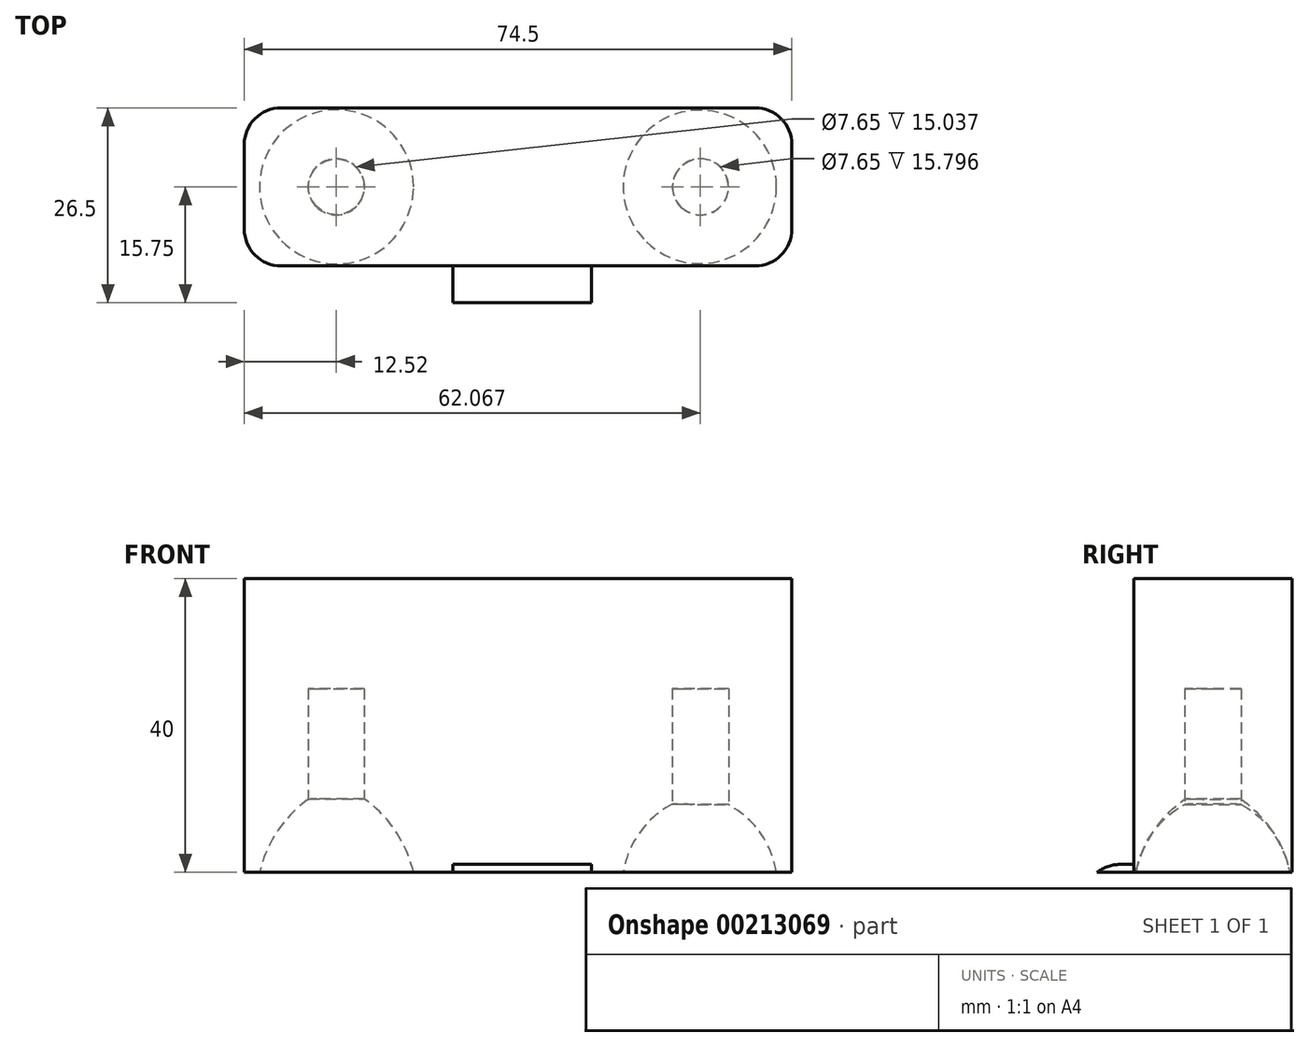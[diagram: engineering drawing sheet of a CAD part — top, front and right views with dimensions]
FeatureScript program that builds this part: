
annotation { "Feature Type Name" : "Feature", "Feature Type Description" : "" }
export const myFeature = defineFeature(function(context is Context, id is Id, definition is map)
    precondition{}
    {
        {
            var Q0;
            Q0=qCreatedBy(makeId("Top.planeOp"),FACE);
            var sketch = newSketch(context, id + "F0", { "sketchPlane" : qUnion([Q0])});
            skLineSegment(sketch, "E0.bottom", {"start": v(-37.25, 10.75) * mm, "end": v(37.25, 10.75) * mm});
            skLineSegment(sketch, "E0.top", {"start": v(-37.25, -10.75) * mm, "end": v(37.25, -10.75) * mm});
            skLineSegment(sketch, "E0.left", {"start": v(-37.25, 10.75) * mm, "end": v(-37.25, -10.75) * mm});
            skLineSegment(sketch, "E0.right", {"start": v(37.25, 10.75) * mm, "end": v(37.25, -10.75) * mm});
            skPoint(sketch, "E1", {"position": v(-37.25, 0) * mm});
            skPoint(sketch, "E2", {"position": v(0, 10.75) * mm});
            skPoint(sketch, "E3", {"position": v(0, -10.75) * mm});
            skPoint(sketch, "E4", {"position": v(37.25, 0) * mm});
            skCircle(sketch, "E5", {"center": v(-24.7, 0) * mm, "radius": 10.55 * mm});
            skCircle(sketch, "E6", {"center": v(24.76, 0) * mm, "radius": 10.55 * mm});
            skLineSegment(sketch, "E7", {"start": v(-24.7, 0) * mm, "end": v(24.76, 0) * mm});
            skSolve(sketch);
        }
        {
            var Q0;
            Q0=makeQuery(id+"F0.imprint","IMPRINT",FACE,{"disambiguationData":[TD([[makeQuery(id+"F0.imprint","IMPRINT",EDGE,{"derivedFrom":sQuery(id+"F0.wireOp",EDGE,"E0.bottom")}),-1.0]])]});
            var Q1;
            Q1=makeQuery(id+"F0.imprint","IMPRINT",FACE,{"disambiguationData":[TD([[makeQuery(id+"F0.imprint","IMPRINT",EDGE,{"derivedFrom":sQuery(id+"F0.wireOp",EDGE,"E5")}),1.0]])]});
            var Q2;
            Q2=makeQuery(id+"F0.imprint","IMPRINT",FACE,{"disambiguationData":[TD([[makeQuery(id+"F0.imprint","IMPRINT",EDGE,{"derivedFrom":sQuery(id+"F0.wireOp",EDGE,"E6")}),1.0]])]});
            extrude(context, id + "F1", {"entities" : qUnion([Q0, Q1, Q2]), "depth" : 40 * mm});
        }
        {
            var Q0;
            Q0=makeQuery(id+"F1.opExtrude","SWEPT_EDGE",EDGE,{"disambiguationData":[OSD([sQuery(id+"F0.wireOp",EDGE,"E0.top"),sQuery(id+"F0.wireOp",EDGE,"E0.left")])]});
            var Q1;
            Q1=makeQuery(id+"F1.opExtrude","SWEPT_EDGE",EDGE,{"disambiguationData":[OSD([sQuery(id+"F0.wireOp",EDGE,"E0.top"),sQuery(id+"F0.wireOp",EDGE,"E0.right")])]});
            var Q2;
            Q2=makeQuery(id+"F1.opExtrude","SWEPT_EDGE",EDGE,{"disambiguationData":[OSD([sQuery(id+"F0.wireOp",EDGE,"E0.bottom"),sQuery(id+"F0.wireOp",EDGE,"E0.left")])]});
            var Q3;
            Q3=makeQuery(id+"F1.opExtrude","SWEPT_EDGE",EDGE,{"disambiguationData":[OSD([sQuery(id+"F0.wireOp",EDGE,"E0.bottom"),sQuery(id+"F0.wireOp",EDGE,"E0.right")])]});
            fillet(context, id + "F2", {"entities" : qUnion([Q0, Q1, Q2, Q3]), "radius" : 5 * mm, "tangentPropagation" : true, "allowEdgeOverflow" : false});
        }
        {
            var Q0;
            Q0=qCreatedBy(makeId("Front.planeOp"),FACE);
            var sketch = newSketch(context, id + "F3", { "sketchPlane" : qUnion([Q0])});
            skPoint(sketch, "E8", {"position": v(-24.7, 0) * mm});
            skLineSegment(sketch, "E9", {"start": v(-24.7, 0) * mm, "end": v(-24.7, 18.44) * mm, "construction": true});
            skLineSegment(sketch, "E10", {"start": v(-28.43, 0) * mm, "end": v(-28.43, 10.05) * mm});
            skLineSegment(sketch, "E11", {"start": v(-28.43, 0) * mm, "end": v(-35.17, 0) * mm});
            skArc(sketch, "E12", {"start": v(-28.43, 10.05) * mm, "mid": v(-32.71, 5.64) * mm, "end": v(-35.17, 0) * mm});
            skSolve(sketch);
        }
        {
            var Q0;
            Q0 = qSketchRegion(id + "F3", true);
            var Q1;
            Q1=sQuery(id+"F3.wireOp",EDGE,"E9");
            revolve(context, id + "F4", {"operationType" : NewBodyOperationType.REMOVE, "entities" : qUnion([Q0]), "axis" : qUnion([Q1]), "revolveType" : RevolveType.FULL, "oppositeDirection" : true});
        }
        {
            var Q0;
            Q0=qCreatedBy(makeId("Front.planeOp"),FACE);
            var sketch = newSketch(context, id + "F5", { "sketchPlane" : qUnion([Q0])});
            skLineSegment(sketch, "E13", {"start": v(24.73, 0) * mm, "end": v(24.73, 14.08) * mm, "construction": true});
            skLineSegment(sketch, "E14", {"start": v(28.45, 0) * mm, "end": v(28.45, 9.3) * mm});
            skLineSegment(sketch, "E15", {"start": v(28.45, 0) * mm, "end": v(35.17, 0) * mm});
            skArc(sketch, "E16", {"start": v(35.17, 0) * mm, "mid": v(32.9, 5.45) * mm, "end": v(28.45, 9.3) * mm});
            skSolve(sketch);
        }
        {
            var Q0;
            Q0 = qSketchRegion(id + "F5", true);
            var Q1;
            Q1=sQuery(id+"F5.wireOp",EDGE,"E13");
            revolve(context, id + "F6", {"operationType" : NewBodyOperationType.REMOVE, "entities" : qUnion([Q0]), "axis" : qUnion([Q1]), "revolveType" : RevolveType.FULL, "oppositeDirection" : true});
        }
        {
            var Q0;
            Q0=makeQuery(id+"F1.opExtrude","SWEPT_FACE",FACE,{"disambiguationData":[OSD([sQuery(id+"F0.wireOp",EDGE,"E0.top")])]});
            var sketch = newSketch(context, id + "F7", { "sketchPlane" : qUnion([Q0])});
            skLineSegment(sketch, "E17.bottom", {"start": v(-8.88, 1.09) * mm, "end": v(9.98, 1.09) * mm});
            skLineSegment(sketch, "E17.top", {"start": v(-8.88, 0) * mm, "end": v(9.98, 0) * mm});
            skLineSegment(sketch, "E17.left", {"start": v(-8.88, 1.09) * mm, "end": v(-8.88, 0) * mm});
            skLineSegment(sketch, "E17.right", {"start": v(9.98, 1.09) * mm, "end": v(9.98, 0) * mm});
            skSolve(sketch);
        }
        {
            var Q0;
            Q0=makeQuery(id+"F7.imprint","IMPRINT",FACE,{"disambiguationData":[TD([[makeQuery(id+"F7.imprint","IMPRINT",EDGE,{"derivedFrom":sQuery(id+"F7.wireOp",EDGE,"E17.bottom")}),-1.0]])]});
            extrude(context, id + "F8", {"entities" : qUnion([Q0]), "operationType" : NewBodyOperationType.ADD, "depth" : 5 * mm});
        }
        {
            var Q0;
            Q0=makeQuery(id+"F8.opExtrude","CAP_EDGE",EDGE,{"disambiguationData":[OSD([sQuery(id+"F7.wireOp",EDGE,"E17.bottom")])],"isStart":false});
            fillet(context, id + "F9", {"entities" : qUnion([Q0]), "radius" : 5 * mm, "tangentPropagation" : true, "allowEdgeOverflow" : false});
        }
        {
            var Q0;
            Q0=qCreatedBy(makeId("Top.planeOp"),FACE);
            var sketch = newSketch(context, id + "F10", { "sketchPlane" : qUnion([Q0])});
            skCircle(sketch, "E18", {"center": v(-24.73, 0) * mm, "radius": 3.82 * mm});
            skSolve(sketch);
        }
        {
            var Q0;
            Q0 = qSketchRegion(id + "F10", true);
            extrude(context, id + "F11", {"entities" : qUnion([Q0]), "operationType" : NewBodyOperationType.REMOVE, "depth" : 25 * mm});
        }
        {
            var Q0;
            Q0=qCreatedBy(makeId("Top.planeOp"),FACE);
            var sketch = newSketch(context, id + "F12", { "sketchPlane" : qUnion([Q0])});
            skCircle(sketch, "E19", {"center": v(24.82, 0) * mm, "radius": 3.83 * mm});
            skSolve(sketch);
        }
        {
            var Q0;
            Q0 = qSketchRegion(id + "F12", true);
            var Q1;
            Q1=sQuery(id+"F12.wireOp",EDGE,"E19");
            extrude(context, id + "F13", {"entities" : qUnion([Q0]), "operationType" : NewBodyOperationType.REMOVE, "surfaceEntities" : qUnion([Q1]), "depth" : 25 * mm});
        }
    });
